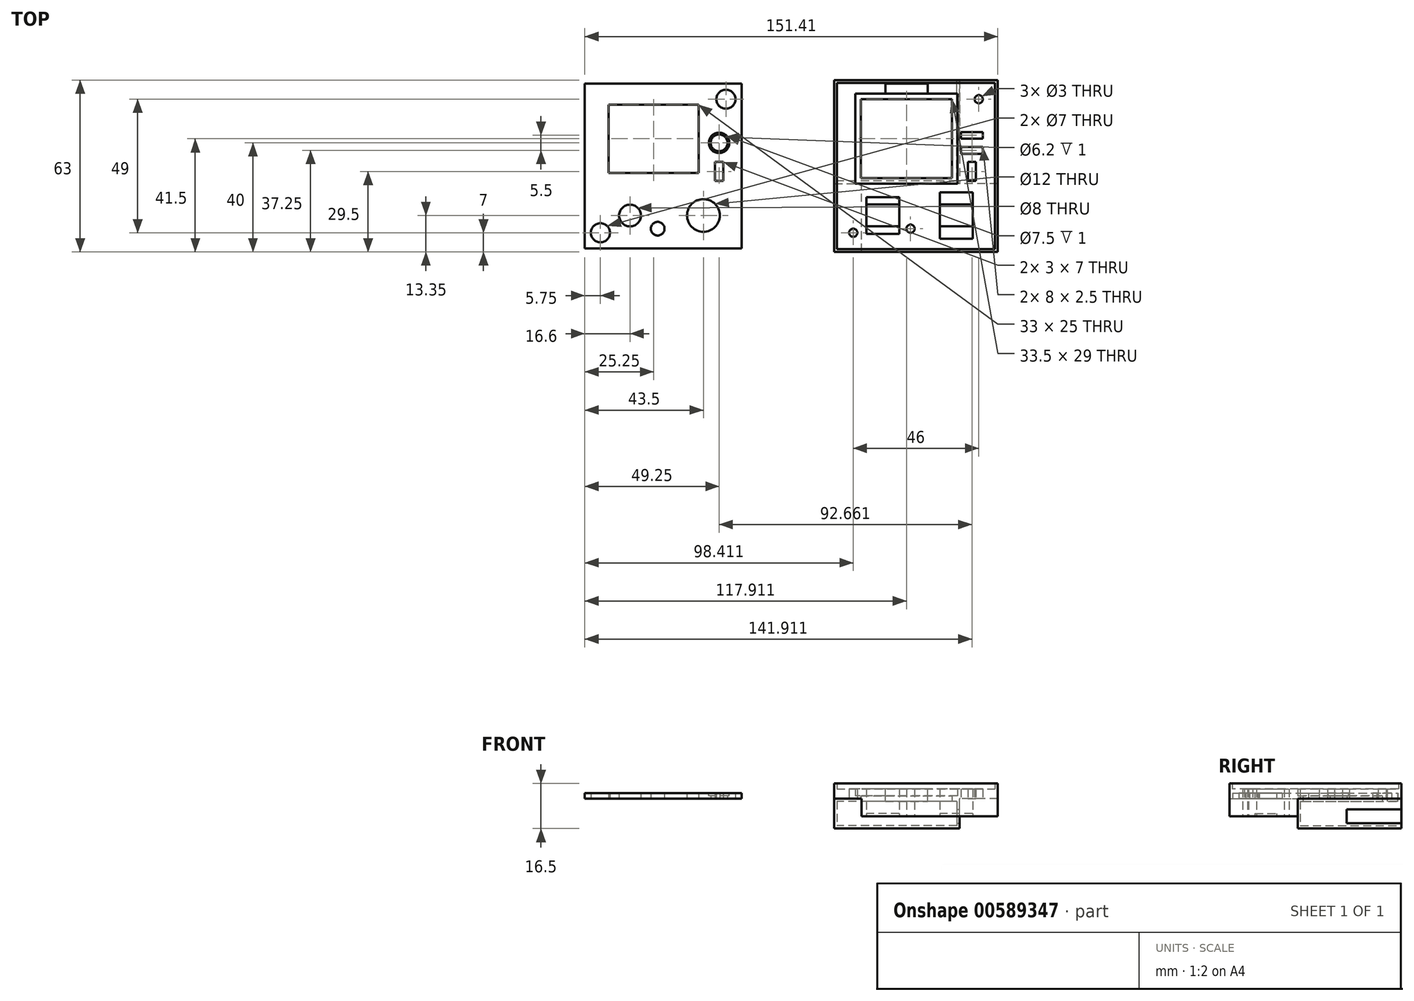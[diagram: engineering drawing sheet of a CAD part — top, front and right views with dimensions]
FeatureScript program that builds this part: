
annotation { "Feature Type Name" : "Feature", "Feature Type Description" : "" }
export const myFeature = defineFeature(function(context is Context, id is Id, definition is map)
    precondition{}
    {
        {
            var Q0;
            Q0=qCreatedBy(makeId("Top.planeOp"),FACE);
            var sketch = newSketch(context, id + "F0", { "sketchPlane" : qUnion([Q0])});
            skPoint(sketch, "E0.middle", {"position": v(0, 0) * mm});
            skLineSegment(sketch, "E1.bottom", {"start": v(13, -2.5) * mm, "end": v(-20, -2.5) * mm});
            skLineSegment(sketch, "E1.top", {"start": v(13, 22.5) * mm, "end": v(-20, 22.5) * mm});
            skLineSegment(sketch, "E1.left", {"start": v(13, -2.5) * mm, "end": v(13, 22.5) * mm});
            skLineSegment(sketch, "E1.right", {"start": v(-20, -2.5) * mm, "end": v(-20, 22.5) * mm});
            skCircle(sketch, "E2", {"center": v(14.75, -18.15) * mm, "radius": 6 * mm});
            skCircle(sketch, "E3", {"center": v(-12.15, -18.15) * mm, "radius": 4 * mm});
            skCircle(sketch, "E4", {"center": v(-2, -23) * mm, "radius": 2.5 * mm});
            skPoint(sketch, "E5", {"position": v(-3.5, 10) * mm});
            skPoint(sketch, "E5.positionSnap0", {"position": v(-3.5, 22.5) * mm});
            skPoint(sketch, "E5.positionSnap1", {"position": v(-20, 10) * mm});
            skCircle(sketch, "E6", {"center": v(-23, -24.5) * mm, "radius": 3.5 * mm});
            skCircle(sketch, "E7", {"center": v(23, 24.5) * mm, "radius": 3.5 * mm});
            skLineSegment(sketch, "E8.bottom", {"start": v(28.75, -30.25) * mm, "end": v(-28.75, -30.25) * mm});
            skLineSegment(sketch, "E8.top", {"start": v(28.75, 30.25) * mm, "end": v(-28.75, 30.25) * mm});
            skLineSegment(sketch, "E8.left", {"start": v(28.75, -30.25) * mm, "end": v(28.75, 30.25) * mm});
            skLineSegment(sketch, "E8.right", {"start": v(-28.75, -30.25) * mm, "end": v(-28.75, 30.25) * mm});
            skCircle(sketch, "E9", {"center": v(20.5, 8.5) * mm, "radius": 3.75 * mm, "construction": true});
            skCircle(sketch, "E10", {"center": v(20.5, 8.5) * mm, "radius": 3.1 * mm});
            skLineSegment(sketch, "E11.bottom", {"start": v(22, -5.5) * mm, "end": v(19, -5.5) * mm});
            skLineSegment(sketch, "E11.top", {"start": v(22, 1.5) * mm, "end": v(19, 1.5) * mm});
            skLineSegment(sketch, "E11.left", {"start": v(22, -5.5) * mm, "end": v(22, 1.5) * mm});
            skLineSegment(sketch, "E11.right", {"start": v(19, -5.5) * mm, "end": v(19, 1.5) * mm});
            skPoint(sketch, "E11.middle", {"position": v(20.5, -2) * mm});
            skSolve(sketch);
        }
        {
            var Q0;
            Q0=qCreatedBy(makeId("Top.planeOp"),FACE);
            var sketch = newSketch(context, id + "F1", { "sketchPlane" : qUnion([Q0])});
            skLineSegment(sketch, "E12.bottom", {"start": v(122.66, -31.5) * mm, "end": v(62.66, -31.5) * mm});
            skLineSegment(sketch, "E12.top", {"start": v(122.66, 31.5) * mm, "end": v(62.66, 31.5) * mm});
            skLineSegment(sketch, "E12.left", {"start": v(122.66, -31.5) * mm, "end": v(122.66, 31.5) * mm});
            skLineSegment(sketch, "E12.right", {"start": v(62.66, -31.5) * mm, "end": v(62.66, 31.5) * mm});
            skPoint(sketch, "E12.middle", {"position": v(92.66, 0) * mm});
            skLineSegment(sketch, "E13.bottom", {"start": v(107.91, -6.5) * mm, "end": v(70.41, -6.5) * mm});
            skLineSegment(sketch, "E13.top", {"start": v(107.91, 26.5) * mm, "end": v(70.41, 26.5) * mm});
            skLineSegment(sketch, "E13.left", {"start": v(107.91, -6.5) * mm, "end": v(107.91, 26.5) * mm});
            skLineSegment(sketch, "E13.right", {"start": v(70.41, -6.5) * mm, "end": v(70.41, 26.5) * mm});
            skCircle(sketch, "E14", {"center": v(69.66, -24.5) * mm, "radius": 1.5 * mm});
            skCircle(sketch, "E15", {"center": v(115.66, 24.5) * mm, "radius": 1.5 * mm});
            skCircle(sketch, "E16", {"center": v(107.41, -18.15) * mm, "radius": 6.1 * mm, "construction": true});
            skLineSegment(sketch, "E17.bottom", {"start": v(111.66, 1.5) * mm, "end": v(114.66, 1.5) * mm});
            skLineSegment(sketch, "E17.top", {"start": v(111.66, -5.5) * mm, "end": v(114.66, -5.5) * mm});
            skLineSegment(sketch, "E17.left", {"start": v(111.66, 1.5) * mm, "end": v(111.66, -5.5) * mm});
            skLineSegment(sketch, "E17.right", {"start": v(114.66, 1.5) * mm, "end": v(114.66, -5.5) * mm});
            skPoint(sketch, "E18.centerSnap0", {"position": v(113.16, 1.5) * mm});
            skCircle(sketch, "E19", {"center": v(80.51, -18.15) * mm, "radius": 2.5 * mm, "construction": true});
            skCircle(sketch, "E20", {"center": v(90.66, -23) * mm, "radius": 1.5 * mm});
            skLineSegment(sketch, "E21.bottom", {"start": v(113.41, -26.65) * mm, "end": v(101.41, -26.65) * mm});
            skLineSegment(sketch, "E21.top", {"start": v(113.41, -9.65) * mm, "end": v(101.41, -9.65) * mm});
            skLineSegment(sketch, "E21.left", {"start": v(113.41, -26.65) * mm, "end": v(113.41, -9.65) * mm});
            skLineSegment(sketch, "E21.right", {"start": v(101.41, -26.65) * mm, "end": v(101.41, -9.65) * mm});
            skLineSegment(sketch, "E22.bottom", {"start": v(115.66, 6) * mm, "end": v(110.66, 6) * mm, "construction": true});
            skLineSegment(sketch, "E22.top", {"start": v(115.66, 11) * mm, "end": v(110.66, 11) * mm, "construction": true});
            skLineSegment(sketch, "E22.left", {"start": v(115.66, 6) * mm, "end": v(115.66, 11) * mm, "construction": true});
            skLineSegment(sketch, "E22.right", {"start": v(110.66, 6) * mm, "end": v(110.66, 11) * mm, "construction": true});
            skPoint(sketch, "E22.middle", {"position": v(113.16, 8.5) * mm});
            skPoint(sketch, "E23", {"position": v(89.16, 10) * mm});
            skPoint(sketch, "E23.positionSnap0", {"position": v(89.16, 26.5) * mm});
            skPoint(sketch, "E23.positionSnap1", {"position": v(70.41, 10) * mm});
            skLineSegment(sketch, "E24.bottom", {"start": v(117.16, 4.5) * mm, "end": v(109.16, 4.5) * mm});
            skLineSegment(sketch, "E24.top", {"start": v(117.16, 12.5) * mm, "end": v(109.16, 12.5) * mm});
            skLineSegment(sketch, "E24.left", {"start": v(117.16, 4.5) * mm, "end": v(117.16, 12.5) * mm});
            skLineSegment(sketch, "E24.right", {"start": v(109.16, 4.5) * mm, "end": v(109.16, 12.5) * mm});
            skCircle(sketch, "E25", {"center": v(69.66, -24.5) * mm, "radius": 3.5 * mm, "construction": true});
            skCircle(sketch, "E26", {"center": v(115.66, 24.5) * mm, "radius": 3.5 * mm, "construction": true});
            skLineSegment(sketch, "E27.bottom", {"start": v(121.41, -30.25) * mm, "end": v(63.91, -30.25) * mm, "construction": true});
            skLineSegment(sketch, "E27.top", {"start": v(121.41, 30.25) * mm, "end": v(63.91, 30.25) * mm, "construction": true});
            skLineSegment(sketch, "E27.left", {"start": v(121.41, -30.25) * mm, "end": v(121.41, 30.25) * mm, "construction": true});
            skLineSegment(sketch, "E27.right", {"start": v(63.91, -30.25) * mm, "end": v(63.91, 30.25) * mm, "construction": true});
            skLineSegment(sketch, "E28.bottom", {"start": v(86.51, -24.9) * mm, "end": v(74.51, -24.9) * mm});
            skLineSegment(sketch, "E28.top", {"start": v(86.51, -11.4) * mm, "end": v(74.51, -11.4) * mm});
            skLineSegment(sketch, "E28.left", {"start": v(86.51, -24.9) * mm, "end": v(86.51, -11.4) * mm});
            skLineSegment(sketch, "E28.right", {"start": v(74.51, -24.9) * mm, "end": v(74.51, -11.4) * mm});
            skLineSegment(sketch, "E29.bottom", {"start": v(86.51, -22.15) * mm, "end": v(74.51, -22.15) * mm});
            skLineSegment(sketch, "E29.top", {"start": v(86.51, -14.15) * mm, "end": v(74.51, -14.15) * mm});
            skLineSegment(sketch, "E29.left", {"start": v(86.51, -22.15) * mm, "end": v(86.51, -14.15) * mm});
            skLineSegment(sketch, "E29.right", {"start": v(74.51, -22.15) * mm, "end": v(74.51, -14.15) * mm});
            skLineSegment(sketch, "E30.bottom", {"start": v(113.41, -22.15) * mm, "end": v(101.41, -22.15) * mm});
            skLineSegment(sketch, "E30.top", {"start": v(113.41, -14.15) * mm, "end": v(101.41, -14.15) * mm});
            skLineSegment(sketch, "E30.left", {"start": v(113.41, -22.15) * mm, "end": v(113.41, -14.15) * mm});
            skLineSegment(sketch, "E30.right", {"start": v(101.41, -22.15) * mm, "end": v(101.41, -14.15) * mm});
            skLineSegment(sketch, "E31.bottom", {"start": v(117.16, 7) * mm, "end": v(109.16, 7) * mm});
            skLineSegment(sketch, "E31.top", {"start": v(117.16, 10) * mm, "end": v(109.16, 10) * mm});
            skLineSegment(sketch, "E31.left", {"start": v(117.16, 7) * mm, "end": v(117.16, 10) * mm});
            skLineSegment(sketch, "E31.right", {"start": v(109.16, 7) * mm, "end": v(109.16, 10) * mm});
            skSolve(sketch);
        }
        {
            var Q0;
            Q0=makeQuery(id+"F1.imprint","IMPRINT",FACE,{"disambiguationData":[TD([[makeQuery(id+"F1.imprint","IMPRINT",EDGE,{"derivedFrom":sQuery(id+"F1.wireOp",EDGE,"E12.bottom")}),-1.0]])]});
            var Q1;
            Q1=makeQuery(id+"F1.imprint","IMPRINT",FACE,{"disambiguationData":[TD([[makeQuery(id+"F1.imprint","IMPRINT",EDGE,{"derivedFrom":sQuery(id+"F1.wireOp",EDGE,"E29.bottom")}),-1.0]])]});
            var Q2;
            Q2=makeQuery(id+"F1.imprint","IMPRINT",FACE,{"disambiguationData":[TD([[makeQuery(id+"F1.imprint","IMPRINT",EDGE,{"derivedFrom":sQuery(id+"F1.wireOp",EDGE,"E30.bottom")}),-1.0]])]});
            var Q3;
            Q3=makeQuery(id+"F1.imprint","IMPRINT",FACE,{"disambiguationData":[TD([[makeQuery(id+"F1.imprint","IMPRINT",EDGE,{"derivedFrom":sQuery(id+"F1.wireOp",EDGE,"E31.bottom")}),-1.0]])]});
            extrude(context, id + "F2", {"entities" : qUnion([Q0, Q1, Q2, Q3]), "depth" : 3.5 * mm});
        }
        {
            var Q0;
            Q0=makeQuery(id+"F2.opExtrude","CAP_FACE",FACE,{"disambiguationData":[OSD([sQuery(id+"F1.wireOp",EDGE,"E12.bottom"),sQuery(id+"F1.wireOp",EDGE,"E12.top"),sQuery(id+"F1.wireOp",EDGE,"E12.left"),sQuery(id+"F1.wireOp",EDGE,"E12.right"),sQuery(id+"F1.wireOp",EDGE,"E13.bottom"),sQuery(id+"F1.wireOp",EDGE,"E13.top"),sQuery(id+"F1.wireOp",EDGE,"E13.left"),sQuery(id+"F1.wireOp",EDGE,"E13.right"),sQuery(id+"F1.wireOp",EDGE,"E14"),sQuery(id+"F1.wireOp",EDGE,"E15"),sQuery(id+"F1.wireOp",EDGE,"E16"),sQuery(id+"F1.wireOp",EDGE,"E17.bottom"),sQuery(id+"F1.wireOp",EDGE,"E17.top"),sQuery(id+"F1.wireOp",EDGE,"E17.left"),sQuery(id+"F1.wireOp",EDGE,"E17.right"),sQuery(id+"F1.wireOp",EDGE,"E18"),sQuery(id+"F1.wireOp",EDGE,"E19"),sQuery(id+"F1.wireOp",EDGE,"E20")])],"isStart":false});
            var sketch = newSketch(context, id + "F3", { "sketchPlane" : qUnion([Q0])});
            skLineSegment(sketch, "E32.bottom", {"start": v(96.91, 26.5) * mm, "end": v(81.41, 26.5) * mm});
            skLineSegment(sketch, "E32.top", {"start": v(96.91, 30.25) * mm, "end": v(81.41, 30.25) * mm});
            skLineSegment(sketch, "E32.left", {"start": v(96.91, 26.5) * mm, "end": v(96.91, 30.25) * mm});
            skLineSegment(sketch, "E32.right", {"start": v(81.41, 26.5) * mm, "end": v(81.41, 30.25) * mm});
            skPoint(sketch, "E32.middle", {"position": v(89.16, 28.38) * mm});
            skPoint(sketch, "E32.middle.positionSnap0", {"position": v(89.16, 26.5) * mm});
            skPoint(sketch, "E32.centerSnap0", {"position": v(89.16, 26.5) * mm});
            skSolve(sketch);
        }
        {
            var Q0;
            Q0=makeQuery(id+"F2.opExtrude","CAP_FACE",FACE,{"disambiguationData":[OSD([sQuery(id+"F1.wireOp",EDGE,"E12.bottom"),sQuery(id+"F1.wireOp",EDGE,"E12.top"),sQuery(id+"F1.wireOp",EDGE,"E12.left"),sQuery(id+"F1.wireOp",EDGE,"E12.right"),sQuery(id+"F1.wireOp",EDGE,"E13.bottom"),sQuery(id+"F1.wireOp",EDGE,"E13.top"),sQuery(id+"F1.wireOp",EDGE,"E13.left"),sQuery(id+"F1.wireOp",EDGE,"E13.right"),sQuery(id+"F1.wireOp",EDGE,"E14"),sQuery(id+"F1.wireOp",EDGE,"E15"),sQuery(id+"F1.wireOp",EDGE,"E16"),sQuery(id+"F1.wireOp",EDGE,"E17.bottom"),sQuery(id+"F1.wireOp",EDGE,"E17.top"),sQuery(id+"F1.wireOp",EDGE,"E17.left"),sQuery(id+"F1.wireOp",EDGE,"E17.right"),sQuery(id+"F1.wireOp",EDGE,"E18"),sQuery(id+"F1.wireOp",EDGE,"E19"),sQuery(id+"F1.wireOp",EDGE,"E20")])],"isStart":true});
            var sketch = newSketch(context, id + "F4", { "sketchPlane" : qUnion([Q0])});
            skLineSegment(sketch, "E33.bottom", {"start": v(70.41, -26.5) * mm, "end": v(107.91, -26.5) * mm});
            skLineSegment(sketch, "E33.top", {"start": v(70.41, 6.5) * mm, "end": v(107.91, 6.5) * mm});
            skLineSegment(sketch, "E33.left", {"start": v(70.41, -26.5) * mm, "end": v(70.41, 6.5) * mm});
            skLineSegment(sketch, "E33.right", {"start": v(107.91, -26.5) * mm, "end": v(107.91, 6.5) * mm});
            skLineSegment(sketch, "E34.0", {"start": v(105.91, -24.5) * mm, "end": v(105.91, 4.5) * mm});
            skLineSegment(sketch, "E34.1", {"start": v(72.41, -24.5) * mm, "end": v(105.91, -24.5) * mm});
            skLineSegment(sketch, "E34.2", {"start": v(72.41, -24.5) * mm, "end": v(72.41, 4.5) * mm});
            skLineSegment(sketch, "E34.3", {"start": v(72.41, 4.5) * mm, "end": v(105.91, 4.5) * mm});
            skSolve(sketch);
        }
        {
            var Q0;
            Q0=makeQuery(id+"F4.imprint","IMPRINT",FACE,{"disambiguationData":[TD([[makeQuery(id+"F4.imprint","IMPRINT",EDGE,{"derivedFrom":sQuery(id+"F4.wireOp",EDGE,"E33.bottom")}),-1.0]])]});
            extrude(context, id + "F5", {"entities" : qUnion([Q0]), "operationType" : NewBodyOperationType.ADD, "oppositeDirection" : true, "depth" : 1 * mm});
        }
        {
            var Q0;
            Q0=makeQuery(id+"F3.imprint","IMPRINT",FACE,{"disambiguationData":[TD([[makeQuery(id+"F3.imprint","IMPRINT",EDGE,{"derivedFrom":sQuery(id+"F3.wireOp",EDGE,"E32.bottom")}),-1.0]])]});
            extrude(context, id + "F6", {"entities" : qUnion([Q0]), "operationType" : NewBodyOperationType.REMOVE, "oppositeDirection" : true, "depth" : 2.5 * mm});
        }
        {
            var Q0;
            Q0=makeQuery(id+"F5.boolean.opBoolean","MERGE",FACE,{"derivedFrom":[makeQuery(id+"F2.opExtrude","CAP_FACE",FACE,{"disambiguationData":[OSD([sQuery(id+"F1.wireOp",EDGE,"E12.bottom"),sQuery(id+"F1.wireOp",EDGE,"E12.top"),sQuery(id+"F1.wireOp",EDGE,"E12.left"),sQuery(id+"F1.wireOp",EDGE,"E12.right"),sQuery(id+"F1.wireOp",EDGE,"E13.bottom"),sQuery(id+"F1.wireOp",EDGE,"E13.top"),sQuery(id+"F1.wireOp",EDGE,"E13.left"),sQuery(id+"F1.wireOp",EDGE,"E13.right"),sQuery(id+"F1.wireOp",EDGE,"E14"),sQuery(id+"F1.wireOp",EDGE,"E15"),sQuery(id+"F1.wireOp",EDGE,"E16"),sQuery(id+"F1.wireOp",EDGE,"E17.bottom"),sQuery(id+"F1.wireOp",EDGE,"E17.top"),sQuery(id+"F1.wireOp",EDGE,"E17.left"),sQuery(id+"F1.wireOp",EDGE,"E17.right"),sQuery(id+"F1.wireOp",EDGE,"E18"),sQuery(id+"F1.wireOp",EDGE,"E19"),sQuery(id+"F1.wireOp",EDGE,"E20")])],"isStart":true}),makeQuery(id+"F5.opExtrude","CAP_FACE",FACE,{"disambiguationData":[OSD([sQuery(id+"F4.wireOp",EDGE,"E33.bottom"),sQuery(id+"F4.wireOp",EDGE,"E33.top"),sQuery(id+"F4.wireOp",EDGE,"E33.left"),sQuery(id+"F4.wireOp",EDGE,"E33.right"),sQuery(id+"F4.wireOp",EDGE,"E34.0"),sQuery(id+"F4.wireOp",EDGE,"E34.1"),sQuery(id+"F4.wireOp",EDGE,"E34.2"),sQuery(id+"F4.wireOp",EDGE,"E34.3")])],"isStart":true})]});
            var sketch = newSketch(context, id + "F7", { "sketchPlane" : qUnion([Q0])});
            skLineSegment(sketch, "E35.bottom", {"start": v(114.91, -31.5) * mm, "end": v(67.91, -31.5) * mm, "construction": true});
            skLineSegment(sketch, "E35.top", {"start": v(114.91, 0.5) * mm, "end": v(67.91, 0.5) * mm, "construction": true});
            skLineSegment(sketch, "E35.left", {"start": v(114.91, -31.5) * mm, "end": v(114.91, 0.5) * mm, "construction": true});
            skLineSegment(sketch, "E35.right", {"start": v(67.91, -31.5) * mm, "end": v(67.91, 0.5) * mm, "construction": true});
            skSolve(sketch);
        }
        {
            var Q0;
            Q0=makeQuery(id+"F0.imprint","IMPRINT",FACE,{"disambiguationData":[TD([[makeQuery(id+"F0.imprint","IMPRINT",EDGE,{"derivedFrom":sQuery(id+"F0.wireOp",EDGE,"E1.bottom")}),1.0]])]});
            var Q1;
            {var subQ3=sQuery(id+"F0.wireOp",EDGE,"XrDQp62H-MWh6-TRDE-LRBF-NnkS5WIpAHLl.bottom");Q1=makeQuery(id+"F0.imprint","IMPRINT",FACE,{"disambiguationData":[TD([[makeQuery(id+"F0.imprint","IMPRINT",EDGE,{"derivedFrom":subQ3}),-1.0]])]});}
            var Q2;
            {var subQ0=sQuery(id+"F0.wireOp",EDGE,"2c6vpU0J-e8TA-CdwJ-wqkp-RvG89t70vTgT.bottom");Q2=makeQuery(id+"F0.imprint","IMPRINT",FACE,{"disambiguationData":[TD([[makeQuery(id+"F0.imprint","IMPRINT",EDGE,{"derivedFrom":subQ0}),1.0]])]});}
            var Q3;
            {var subQ3=sQuery(id+"F0.wireOp",EDGE,"BUTc56Jz-DEV2-YpXM-oIQJ-WA8c8EbTXwWs.bottom");Q3=makeQuery(id+"F0.imprint","IMPRINT",FACE,{"disambiguationData":[TD([[makeQuery(id+"F0.imprint","IMPRINT",EDGE,{"derivedFrom":subQ3}),1.0]])]});}
            var Q4;
            {var subQ0=sQuery(id+"F0.wireOp",EDGE,"JL6GV5r3-Ixaj-ni79-uZlj-3xSKczFOYfCu.bottom");Q4=makeQuery(id+"F0.imprint","IMPRINT",FACE,{"disambiguationData":[TD([[makeQuery(id+"F0.imprint","IMPRINT",EDGE,{"derivedFrom":subQ0}),-1.0]])]});}
            extrude(context, id + "F8", {"entities" : qUnion([Q0, Q1, Q2, Q3, Q4]), "depth" : 2 * mm});
        }
        {
            var Q0;
            Q0=makeQuery(id+"F8.opExtrude","CAP_FACE",FACE,{"disambiguationData":[OSD([sQuery(id+"F0.wireOp",EDGE,"E1.bottom"),sQuery(id+"F0.wireOp",EDGE,"E1.top"),sQuery(id+"F0.wireOp",EDGE,"E1.left"),sQuery(id+"F0.wireOp",EDGE,"E1.right"),sQuery(id+"F0.wireOp",EDGE,"2c6vpU0J-e8TA-CdwJ-wqkp-RvG89t70vTgT.top"),sQuery(id+"F0.wireOp",EDGE,"JL6GV5r3-Ixaj-ni79-uZlj-3xSKczFOYfCu.top"),sQuery(id+"F0.wireOp",EDGE,"XrDQp62H-MWh6-TRDE-LRBF-NnkS5WIpAHLl.bottom"),sQuery(id+"F0.wireOp",EDGE,"XrDQp62H-MWh6-TRDE-LRBF-NnkS5WIpAHLl.top"),sQuery(id+"F0.wireOp",EDGE,"XrDQp62H-MWh6-TRDE-LRBF-NnkS5WIpAHLl.right"),sQuery(id+"F0.wireOp",EDGE,"BUTc56Jz-DEV2-YpXM-oIQJ-WA8c8EbTXwWs.bottom"),sQuery(id+"F0.wireOp",EDGE,"BUTc56Jz-DEV2-YpXM-oIQJ-WA8c8EbTXwWs.top"),sQuery(id+"F0.wireOp",EDGE,"BUTc56Jz-DEV2-YpXM-oIQJ-WA8c8EbTXwWs.right"),sQuery(id+"F0.wireOp",EDGE,"E2"),sQuery(id+"F0.wireOp",EDGE,"E3"),sQuery(id+"F0.wireOp",EDGE,"E4")])],"isStart":false});
            var sketch = newSketch(context, id + "F9", { "sketchPlane" : qUnion([Q0])});
            skLineSegment(sketch, "E36.bottom", {"start": v(-20, 22.5) * mm, "end": v(13, 22.5) * mm});
            skLineSegment(sketch, "E36.top", {"start": v(-20, 23.5) * mm, "end": v(13, 23.5) * mm});
            skLineSegment(sketch, "E36.left", {"start": v(-20, 22.5) * mm, "end": v(-20, 23.5) * mm});
            skLineSegment(sketch, "E36.right", {"start": v(13, 22.5) * mm, "end": v(13, 23.5) * mm});
            skLineSegment(sketch, "E37.bottom", {"start": v(-20, 23.5) * mm, "end": v(-21, 23.5) * mm});
            skLineSegment(sketch, "E37.top", {"start": v(-20, -2.5) * mm, "end": v(-21, -2.5) * mm});
            skLineSegment(sketch, "E37.left", {"start": v(-20, 23.5) * mm, "end": v(-20, -2.5) * mm});
            skLineSegment(sketch, "E37.right", {"start": v(-21, 23.5) * mm, "end": v(-21, -2.5) * mm});
            skLineSegment(sketch, "E38.bottom", {"start": v(13, 23.5) * mm, "end": v(14, 23.5) * mm});
            skLineSegment(sketch, "E38.top", {"start": v(13, -2.5) * mm, "end": v(14, -2.5) * mm});
            skLineSegment(sketch, "E38.left", {"start": v(13, 23.5) * mm, "end": v(13, -2.5) * mm});
            skLineSegment(sketch, "E38.right", {"start": v(14, 23.5) * mm, "end": v(14, -2.5) * mm});
            skLineSegment(sketch, "E39.bottom", {"start": v(-21, -2.5) * mm, "end": v(14, -2.5) * mm});
            skLineSegment(sketch, "E39.top", {"start": v(-21, -3.5) * mm, "end": v(14, -3.5) * mm});
            skLineSegment(sketch, "E39.left", {"start": v(-21, -2.5) * mm, "end": v(-21, -3.5) * mm});
            skLineSegment(sketch, "E39.right", {"start": v(14, -2.5) * mm, "end": v(14, -3.5) * mm});
            skSolve(sketch);
        }
        {
            var Q0;
            Q0=makeQuery(id+"F7.imprint","IMPRINT",FACE,{"disambiguationData":[TD([[makeQuery(id+"F7.imprint","IMPRINT",EDGE,{"derivedFrom":makeQuery(id+"F2.opExtrude","CAP_EDGE",EDGE,{"disambiguationData":[OSD([sQuery(id+"F1.wireOp",EDGE,"E12.bottom")])],"isStart":true})}),1.0]])]});
            var sketch = newSketch(context, id + "F10", { "sketchPlane" : qUnion([Q0])});
            skPoint(sketch, "E40.0", {"position": v(62.66, -31.5) * mm});
            skPoint(sketch, "E41.0", {"position": v(122.66, -31.5) * mm});
            skLineSegment(sketch, "E42.bottom", {"start": v(62.66, -31.5) * mm, "end": v(108.66, -31.5) * mm});
            skLineSegment(sketch, "E42.top", {"start": v(62.66, 6.5) * mm, "end": v(108.66, 6.5) * mm});
            skLineSegment(sketch, "E42.left", {"start": v(62.66, -31.5) * mm, "end": v(62.66, 6.5) * mm});
            skLineSegment(sketch, "E42.right", {"start": v(108.66, -31.5) * mm, "end": v(108.66, 6.5) * mm});
            skSolve(sketch);
        }
        {
            var Q0;
            Q0=qSketchRegion(id+"F10",true);
            extrude(context, id + "F11", {"entities" : qUnion([Q0]), "operationType" : NewBodyOperationType.ADD, "depth" : 11 * mm});
        }
        {
            var Q0;
            Q0=makeQuery(id+"F11.boolean.opBoolean","MERGE",FACE,{"derivedFrom":[makeQuery(id+"F2.opExtrude","SWEPT_FACE",FACE,{"disambiguationData":[OSD([sQuery(id+"F1.wireOp",EDGE,"E12.top")])]}),makeQuery(id+"F11.opExtrude","SWEPT_FACE",FACE,{"disambiguationData":[OSD([sQuery(id+"F10.wireOp",EDGE,"E42.bottom")])]})]});
            var sketch = newSketch(context, id + "F12", { "sketchPlane" : qUnion([Q0])});
            skLineSegment(sketch, "E43.bottom", {"start": v(-107.66, -1) * mm, "end": v(-63.66, -1) * mm});
            skLineSegment(sketch, "E43.top", {"start": v(-107.66, -10) * mm, "end": v(-63.66, -10) * mm});
            skLineSegment(sketch, "E43.left", {"start": v(-107.66, -1) * mm, "end": v(-107.66, -10) * mm});
            skLineSegment(sketch, "E43.right", {"start": v(-63.66, -1) * mm, "end": v(-63.66, -10) * mm});
            skSolve(sketch);
        }
        {
            var Q0;
            Q0=qSketchRegion(id+"F12",true);
            extrude(context, id + "F13", {"entities" : qUnion([Q0]), "operationType" : NewBodyOperationType.REMOVE, "oppositeDirection" : true, "depth" : 37 * mm});
        }
        {
            var Q0;
            Q0=makeQuery(id+"F11.boolean.opBoolean","MERGE",FACE,{"derivedFrom":[makeQuery(id+"F2.opExtrude","SWEPT_FACE",FACE,{"disambiguationData":[OSD([sQuery(id+"F1.wireOp",EDGE,"E12.top")])]}),makeQuery(id+"F11.opExtrude","SWEPT_FACE",FACE,{"disambiguationData":[OSD([sQuery(id+"F10.wireOp",EDGE,"E42.bottom")])]})]});
            var sketch = newSketch(context, id + "F14", { "sketchPlane" : qUnion([Q0])});
            skLineSegment(sketch, "E44.bottom", {"start": v(-107.66, -9) * mm, "end": v(-108.66, -9) * mm});
            skLineSegment(sketch, "E44.top", {"start": v(-107.66, -4) * mm, "end": v(-108.66, -4) * mm});
            skLineSegment(sketch, "E44.left", {"start": v(-107.66, -9) * mm, "end": v(-107.66, -4) * mm});
            skLineSegment(sketch, "E44.right", {"start": v(-108.66, -9) * mm, "end": v(-108.66, -4) * mm});
            skSolve(sketch);
        }
        {
            var Q0;
            Q0=qSketchRegion(id+"F14",true);
            extrude(context, id + "F15", {"entities" : qUnion([Q0]), "operationType" : NewBodyOperationType.REMOVE, "oppositeDirection" : true, "depth" : 20 * mm});
        }
        {
            var Q0;
            Q0=makeQuery(id+"F6.boolean.opBoolean","MERGE",FACE,{"derivedFrom":[makeQuery(id+"F5.opExtrude","CAP_FACE",FACE,{"disambiguationData":[OSD([sQuery(id+"F4.wireOp",EDGE,"E33.bottom"),sQuery(id+"F4.wireOp",EDGE,"E33.top"),sQuery(id+"F4.wireOp",EDGE,"E33.left"),sQuery(id+"F4.wireOp",EDGE,"E33.right"),sQuery(id+"F4.wireOp",EDGE,"E34.0"),sQuery(id+"F4.wireOp",EDGE,"E34.1"),sQuery(id+"F4.wireOp",EDGE,"E34.2"),sQuery(id+"F4.wireOp",EDGE,"E34.3")])],"isStart":false}),makeQuery(id+"F6.opExtrude","CAP_FACE",FACE,{"disambiguationData":[OSD([sQuery(id+"F3.wireOp",EDGE,"E32.bottom"),sQuery(id+"F3.wireOp",EDGE,"E32.top"),sQuery(id+"F3.wireOp",EDGE,"E32.left"),sQuery(id+"F3.wireOp",EDGE,"E32.right")])],"isStart":false})]});
            var sketch = newSketch(context, id + "F16", { "sketchPlane" : qUnion([Q0])});
            skPoint(sketch, "E45.0", {"position": v(72.41, 24.5) * mm});
            skPoint(sketch, "E45.1", {"position": v(105.91, -4.5) * mm});
            skLineSegment(sketch, "E46.bottom", {"start": v(72.41, 24.5) * mm, "end": v(105.91, 24.5) * mm});
            skLineSegment(sketch, "E46.top", {"start": v(72.41, -4.5) * mm, "end": v(105.91, -4.5) * mm});
            skLineSegment(sketch, "E46.left", {"start": v(72.41, -4.5) * mm, "end": v(72.41, 24.5) * mm});
            skLineSegment(sketch, "E46.right", {"start": v(105.91, -4.5) * mm, "end": v(105.91, 24.5) * mm});
            skLineSegment(sketch, "E47.bottom", {"start": v(81.41, 30.25) * mm, "end": v(96.91, 30.25) * mm});
            skLineSegment(sketch, "E47.top", {"start": v(81.41, 26.5) * mm, "end": v(96.91, 26.5) * mm});
            skLineSegment(sketch, "E47.left", {"start": v(81.41, 30.25) * mm, "end": v(81.41, 26.5) * mm});
            skLineSegment(sketch, "E47.right", {"start": v(96.91, 30.25) * mm, "end": v(96.91, 26.5) * mm});
            skSolve(sketch);
        }
        {
            var Q0;
            Q0=qSketchRegion(id+"F16",true);
            extrude(context, id + "F17", {"entities" : qUnion([Q0]), "operationType" : NewBodyOperationType.REMOVE, "oppositeDirection" : true, "depth" : 4 * mm});
        }
        {
            var Q0;
            Q0=makeQuery(id+"F2.opExtrude","CAP_FACE",FACE,{"disambiguationData":[OSD([sQuery(id+"F1.wireOp",EDGE,"E12.bottom"),sQuery(id+"F1.wireOp",EDGE,"E12.top"),sQuery(id+"F1.wireOp",EDGE,"E12.left"),sQuery(id+"F1.wireOp",EDGE,"E12.right"),sQuery(id+"F1.wireOp",EDGE,"E13.bottom"),sQuery(id+"F1.wireOp",EDGE,"E13.top"),sQuery(id+"F1.wireOp",EDGE,"E13.left"),sQuery(id+"F1.wireOp",EDGE,"E13.right"),sQuery(id+"F1.wireOp",EDGE,"E14"),sQuery(id+"F1.wireOp",EDGE,"E15"),sQuery(id+"F1.wireOp",EDGE,"E17.bottom"),sQuery(id+"F1.wireOp",EDGE,"E17.top"),sQuery(id+"F1.wireOp",EDGE,"E17.left"),sQuery(id+"F1.wireOp",EDGE,"E17.right"),sQuery(id+"F1.wireOp",EDGE,"E19"),sQuery(id+"F1.wireOp",EDGE,"E20"),sQuery(id+"F1.wireOp",EDGE,"E21.bottom"),sQuery(id+"F1.wireOp",EDGE,"E21.top"),sQuery(id+"F1.wireOp",EDGE,"E21.left"),sQuery(id+"F1.wireOp",EDGE,"E21.right"),sQuery(id+"F1.wireOp",EDGE,"E24.bottom"),sQuery(id+"F1.wireOp",EDGE,"E24.top"),sQuery(id+"F1.wireOp",EDGE,"E24.left"),sQuery(id+"F1.wireOp",EDGE,"E24.right")])],"isStart":false});
            var sketch = newSketch(context, id + "F18", { "sketchPlane" : qUnion([Q0])});
            skLineSegment(sketch, "E48.bottom", {"start": v(62.66, 31.5) * mm, "end": v(122.66, 31.5) * mm});
            skLineSegment(sketch, "E48.top", {"start": v(62.66, -31.5) * mm, "end": v(122.66, -31.5) * mm});
            skLineSegment(sketch, "E48.left", {"start": v(62.66, 31.5) * mm, "end": v(62.66, -31.5) * mm});
            skLineSegment(sketch, "E48.right", {"start": v(122.66, 31.5) * mm, "end": v(122.66, -31.5) * mm});
            skLineSegment(sketch, "E49.0", {"start": v(63.66, -30.5) * mm, "end": v(121.66, -30.5) * mm});
            skLineSegment(sketch, "E49.1", {"start": v(63.66, 30.5) * mm, "end": v(63.66, -30.5) * mm});
            skLineSegment(sketch, "E49.2", {"start": v(63.66, 30.5) * mm, "end": v(121.66, 30.5) * mm});
            skLineSegment(sketch, "E49.3", {"start": v(121.66, 30.5) * mm, "end": v(121.66, -30.5) * mm});
            skSolve(sketch);
        }
        {
            var Q0;
            Q0=qSketchRegion(id+"F18",true);
            extrude(context, id + "F19", {"entities" : qUnion([Q0]), "operationType" : NewBodyOperationType.ADD, "depth" : 2 * mm});
        }
        {
            var Q0;
            Q0=makeQuery(id+"F7.imprint","IMPRINT",FACE,{"disambiguationData":[TD([[makeQuery(id+"F7.imprint","IMPRINT",EDGE,{"derivedFrom":makeQuery(id+"F2.opExtrude","CAP_EDGE",EDGE,{"disambiguationData":[OSD([sQuery(id+"F1.wireOp",EDGE,"E12.bottom")])],"isStart":true})}),1.0]])]});
            var sketch = newSketch(context, id + "F20", { "sketchPlane" : qUnion([Q0])});
            skPoint(sketch, "E50.0", {"position": v(122.66, 31.5) * mm});
            skLineSegment(sketch, "E51.bottom", {"start": v(122.66, 31.5) * mm, "end": v(72.66, 31.5) * mm});
            skLineSegment(sketch, "E51.top", {"start": v(122.66, 6.5) * mm, "end": v(72.66, 6.5) * mm});
            skLineSegment(sketch, "E51.left", {"start": v(122.66, 31.5) * mm, "end": v(122.66, 6.5) * mm});
            skLineSegment(sketch, "E51.right", {"start": v(72.66, 31.5) * mm, "end": v(72.66, 6.5) * mm});
            skPoint(sketch, "E52.0", {"position": v(90.66, 23) * mm});
            skCircle(sketch, "E53", {"center": v(90.66, 23) * mm, "radius": 1.5 * mm});
            skPoint(sketch, "E54.0", {"position": v(74.51, 24.9) * mm});
            skPoint(sketch, "E54.1", {"position": v(86.51, 22.15) * mm});
            skPoint(sketch, "E54.2", {"position": v(86.51, 14.15) * mm});
            skPoint(sketch, "E54.3", {"position": v(74.51, 11.4) * mm});
            skPoint(sketch, "E54.4", {"position": v(101.41, 22.15) * mm});
            skPoint(sketch, "E54.5", {"position": v(113.41, 26.65) * mm});
            skPoint(sketch, "E54.6", {"position": v(113.41, 14.15) * mm});
            skPoint(sketch, "E54.7", {"position": v(101.41, 9.65) * mm});
            skLineSegment(sketch, "E55.bottom", {"start": v(74.51, 24.9) * mm, "end": v(86.51, 24.9) * mm});
            skLineSegment(sketch, "E55.top", {"start": v(74.51, 22.15) * mm, "end": v(86.51, 22.15) * mm});
            skLineSegment(sketch, "E55.left", {"start": v(74.51, 24.9) * mm, "end": v(74.51, 22.15) * mm});
            skLineSegment(sketch, "E55.right", {"start": v(86.51, 24.9) * mm, "end": v(86.51, 22.15) * mm});
            skLineSegment(sketch, "E56.bottom", {"start": v(74.51, 11.4) * mm, "end": v(86.51, 11.4) * mm});
            skLineSegment(sketch, "E56.top", {"start": v(74.51, 14.15) * mm, "end": v(86.51, 14.15) * mm});
            skLineSegment(sketch, "E56.left", {"start": v(74.51, 11.4) * mm, "end": v(74.51, 14.15) * mm});
            skLineSegment(sketch, "E56.right", {"start": v(86.51, 11.4) * mm, "end": v(86.51, 14.15) * mm});
            skLineSegment(sketch, "E57.bottom", {"start": v(101.41, 22.15) * mm, "end": v(113.41, 22.15) * mm});
            skLineSegment(sketch, "E57.top", {"start": v(101.41, 26.65) * mm, "end": v(113.41, 26.65) * mm});
            skLineSegment(sketch, "E57.left", {"start": v(101.41, 22.15) * mm, "end": v(101.41, 26.65) * mm});
            skLineSegment(sketch, "E57.right", {"start": v(113.41, 22.15) * mm, "end": v(113.41, 26.65) * mm});
            skLineSegment(sketch, "E58.bottom", {"start": v(101.41, 9.65) * mm, "end": v(113.41, 9.65) * mm});
            skLineSegment(sketch, "E58.top", {"start": v(101.41, 14.15) * mm, "end": v(113.41, 14.15) * mm});
            skLineSegment(sketch, "E58.left", {"start": v(101.41, 9.65) * mm, "end": v(101.41, 14.15) * mm});
            skLineSegment(sketch, "E58.right", {"start": v(113.41, 9.65) * mm, "end": v(113.41, 14.15) * mm});
            skSolve(sketch);
        }
        {
            var Q0;
            Q0=qSketchRegion(id+"F20",true);
            extrude(context, id + "F21", {"entities" : qUnion([Q0]), "operationType" : NewBodyOperationType.ADD, "depth" : 6.5 * mm});
        }
        {
            var Q0;
            Q0=makeQuery(id+"F2.opExtrude","CAP_FACE",FACE,{"disambiguationData":[OSD([sQuery(id+"F1.wireOp",EDGE,"E12.bottom"),sQuery(id+"F1.wireOp",EDGE,"E12.top"),sQuery(id+"F1.wireOp",EDGE,"E12.left"),sQuery(id+"F1.wireOp",EDGE,"E12.right"),sQuery(id+"F1.wireOp",EDGE,"E13.bottom"),sQuery(id+"F1.wireOp",EDGE,"E13.top"),sQuery(id+"F1.wireOp",EDGE,"E13.left"),sQuery(id+"F1.wireOp",EDGE,"E13.right"),sQuery(id+"F1.wireOp",EDGE,"E14"),sQuery(id+"F1.wireOp",EDGE,"E15"),sQuery(id+"F1.wireOp",EDGE,"E17.bottom"),sQuery(id+"F1.wireOp",EDGE,"E17.top"),sQuery(id+"F1.wireOp",EDGE,"E17.left"),sQuery(id+"F1.wireOp",EDGE,"E17.right"),sQuery(id+"F1.wireOp",EDGE,"E20"),sQuery(id+"F1.wireOp",EDGE,"E21.bottom"),sQuery(id+"F1.wireOp",EDGE,"E21.top"),sQuery(id+"F1.wireOp",EDGE,"E21.left"),sQuery(id+"F1.wireOp",EDGE,"E21.right"),sQuery(id+"F1.wireOp",EDGE,"E24.bottom"),sQuery(id+"F1.wireOp",EDGE,"E24.top"),sQuery(id+"F1.wireOp",EDGE,"E24.left"),sQuery(id+"F1.wireOp",EDGE,"E24.right"),sQuery(id+"F1.wireOp",EDGE,"E28.bottom"),sQuery(id+"F1.wireOp",EDGE,"E28.top"),sQuery(id+"F1.wireOp",EDGE,"E28.left"),sQuery(id+"F1.wireOp",EDGE,"E28.right"),sQuery(id+"F1.wireOp",EDGE,"E29.bottom"),sQuery(id+"F1.wireOp",EDGE,"E29.top"),sQuery(id+"F1.wireOp",EDGE,"E30.bottom"),sQuery(id+"F1.wireOp",EDGE,"E30.top"),sQuery(id+"F1.wireOp",EDGE,"E31.bottom"),sQuery(id+"F1.wireOp",EDGE,"E31.top")])],"isStart":false});
            var sketch = newSketch(context, id + "F22", { "sketchPlane" : qUnion([Q0])});
            skLineSegment(sketch, "E59.bottom", {"start": v(74.51, -11.4) * mm, "end": v(86.51, -11.4) * mm});
            skLineSegment(sketch, "E59.top", {"start": v(74.51, -24.9) * mm, "end": v(86.51, -24.9) * mm});
            skLineSegment(sketch, "E59.left", {"start": v(74.51, -11.4) * mm, "end": v(74.51, -24.9) * mm});
            skLineSegment(sketch, "E59.right", {"start": v(86.51, -11.4) * mm, "end": v(86.51, -24.9) * mm});
            skLineSegment(sketch, "E60.bottom", {"start": v(101.41, -9.65) * mm, "end": v(113.41, -9.65) * mm});
            skLineSegment(sketch, "E60.top", {"start": v(101.41, -26.65) * mm, "end": v(113.41, -26.65) * mm});
            skLineSegment(sketch, "E60.left", {"start": v(101.41, -9.65) * mm, "end": v(101.41, -26.65) * mm});
            skLineSegment(sketch, "E60.right", {"start": v(113.41, -9.65) * mm, "end": v(113.41, -26.65) * mm});
            skSolve(sketch);
        }
        {
            var Q0;
            Q0=qSketchRegion(id+"F22",true);
            extrude(context, id + "F23", {"entities" : qUnion([Q0]), "operationType" : NewBodyOperationType.REMOVE, "oppositeDirection" : true, "depth" : 9 * mm});
        }
        {
            var Q0;
            Q0=makeQuery(id+"F9.imprint","IMPRINT",FACE,{"disambiguationData":[TD([[makeQuery(id+"F9.imprint","IMPRINT",EDGE,{"derivedFrom":sQuery(id+"F9.wireOp",EDGE,"E36.top")}),1.0]])]});
            var sketch = newSketch(context, id + "F26", { "sketchPlane" : qUnion([Q0])});
            skPoint(sketch, "E61.0", {"position": v(20.5, 8.5) * mm});
            skCircle(sketch, "E62", {"center": v(20.5, 8.5) * mm, "radius": 3.75 * mm});
            skSolve(sketch);
        }
        {
            var Q0;
            Q0=qSketchRegion(id+"F26",true);
            extrude(context, id + "F27", {"entities" : qUnion([Q0]), "operationType" : NewBodyOperationType.REMOVE, "oppositeDirection" : true, "depth" : 1 * mm});
        }
    });
